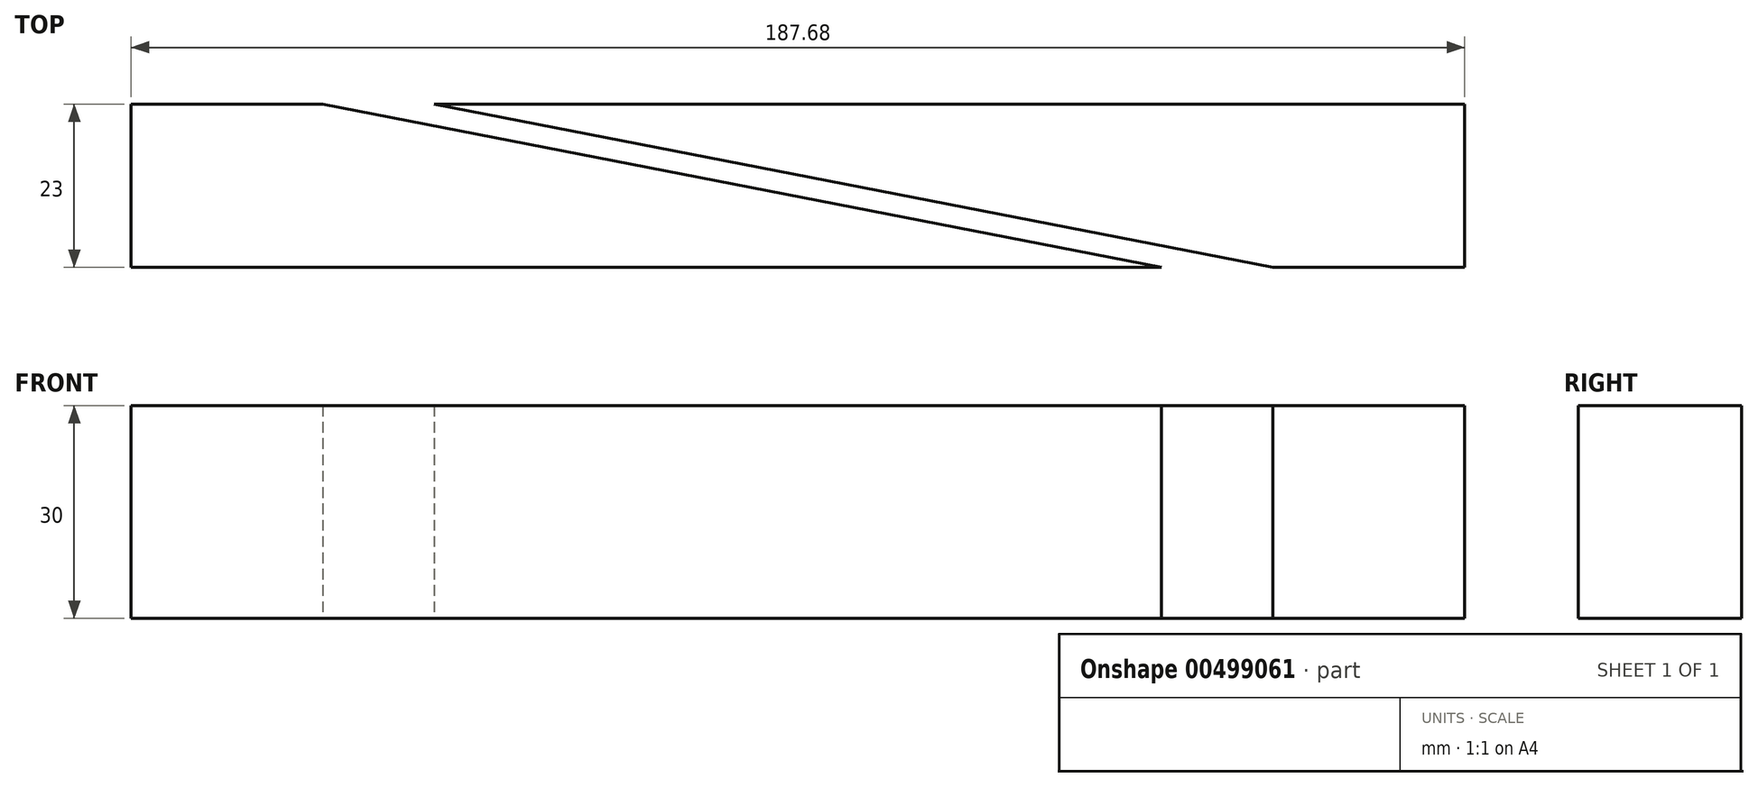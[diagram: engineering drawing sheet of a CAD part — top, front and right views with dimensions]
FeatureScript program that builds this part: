
annotation { "Feature Type Name" : "Feature", "Feature Type Description" : "" }
export const myFeature = defineFeature(function(context is Context, id is Id, definition is map)
    precondition{}
    {
        {
            var Q0;
            Q0=qCreatedBy(makeId("Top.planeOp"),FACE);
            var sketch = newSketch(context, id + "F0", { "sketchPlane" : qUnion([Q0])});
            skLineSegment(sketch, "E0", {"start": v(0, 0) * mm, "end": v(145, 0) * mm, "construction": true});
            skLineSegment(sketch, "E1", {"start": v(145, 0) * mm, "end": v(140, 0) * mm, "construction": true});
            skLineSegment(sketch, "E2", {"start": v(0, 0) * mm, "end": v(0, 23) * mm, "construction": true});
            skLineSegment(sketch, "E3", {"start": v(0, 23) * mm, "end": v(27, 23) * mm, "construction": true});
            skLineSegment(sketch, "E4", {"start": v(27, 23) * mm, "end": v(145, 0) * mm, "construction": true});
            skLineSegment(sketch, "E5", {"start": v(140.28, 0.92) * mm, "end": v(140.86, 3.86) * mm, "construction": true});
            skLineSegment(sketch, "E6", {"start": v(27, 23) * mm, "end": v(27.57, 25.94) * mm, "construction": true});
            skLineSegment(sketch, "E7", {"start": v(27.57, 25.94) * mm, "end": v(175.83, -2.95) * mm, "construction": true});
            skLineSegment(sketch, "E8", {"start": v(145, 0) * mm, "end": v(160.68, 0) * mm, "construction": true});
            skLineSegment(sketch, "E9", {"start": v(160.68, 0) * mm, "end": v(187.68, 0) * mm});
            skLineSegment(sketch, "E10", {"start": v(187.68, 0) * mm, "end": v(187.68, 23) * mm});
            skLineSegment(sketch, "E11", {"start": v(187.68, 23) * mm, "end": v(42.68, 23) * mm});
            skLineSegment(sketch, "E12", {"start": v(42.68, 23) * mm, "end": v(160.68, 0) * mm});
            skLineSegment(sketch, "E13", {"start": v(145, 0) * mm, "end": v(27, 23) * mm});
            skLineSegment(sketch, "E14", {"start": v(0, 23) * mm, "end": v(0, 0) * mm});
            skLineSegment(sketch, "E15", {"start": v(145, 0) * mm, "end": v(0, 0) * mm});
            skLineSegment(sketch, "E16", {"start": v(0, 23) * mm, "end": v(27, 23) * mm});
            skSolve(sketch);
        }
        {
            var Q0;
            Q0 = qSketchRegion(id + "F0", true);
            extrude(context, id + "F1", {"entities" : qUnion([Q0]), "depth" : 30 * mm});
        }
    });
